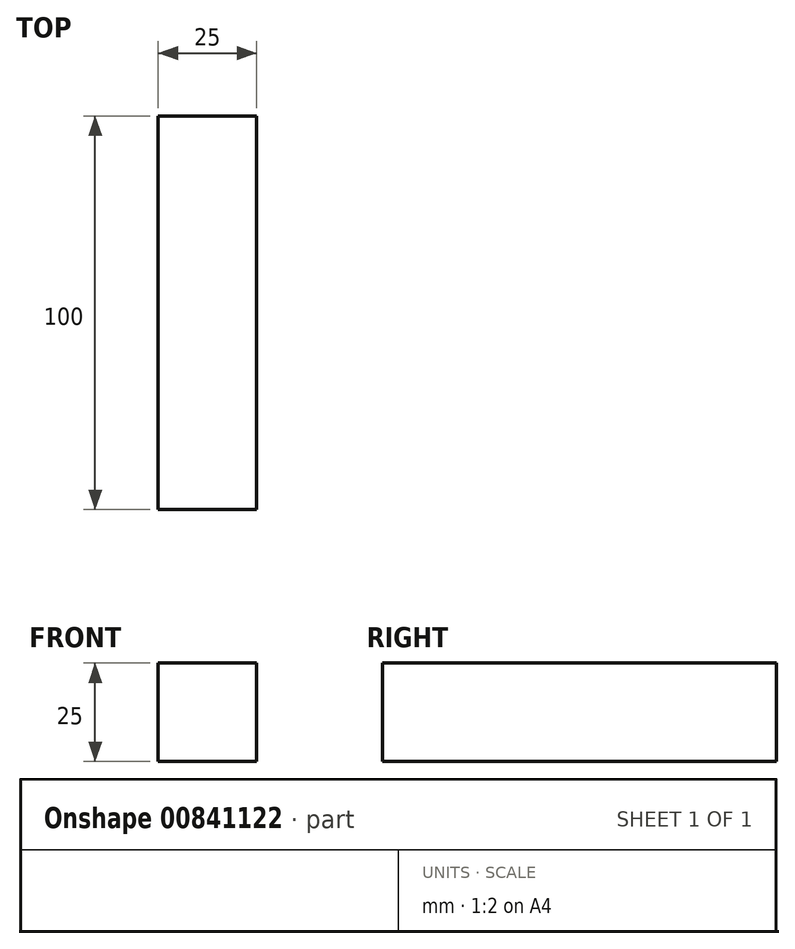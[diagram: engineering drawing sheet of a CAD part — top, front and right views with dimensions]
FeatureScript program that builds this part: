
annotation { "Feature Type Name" : "Feature", "Feature Type Description" : "" }
export const myFeature = defineFeature(function(context is Context, id is Id, definition is map)
    precondition{}
    {
        {
            var Q0;
            Q0=qCreatedBy(makeId("Front.planeOp"),FACE);
            var sketch = newSketch(context, id + "F0", { "sketchPlane" : qUnion([Q0])});
            skLineSegment(sketch, "E0.bottom", {"start": v(12.5, 12.5) * mm, "end": v(-12.5, 12.5) * mm});
            skLineSegment(sketch, "E0.top", {"start": v(12.5, -12.5) * mm, "end": v(-12.5, -12.5) * mm});
            skLineSegment(sketch, "E0.left", {"start": v(12.5, 12.5) * mm, "end": v(12.5, -12.5) * mm});
            skLineSegment(sketch, "E0.right", {"start": v(-12.5, 12.5) * mm, "end": v(-12.5, -12.5) * mm});
            skPoint(sketch, "E0.middle", {"position": v(0, 0) * mm});
            skSolve(sketch);
        }
        {
            var Q0;
            Q0=qSketchRegion(id+"F0",true);
            extrude(context, id + "F1", {"entities" : qUnion([Q0]), "depth" : 100 * mm, "offsetDistance" : 25 * mm});
        }
    });
